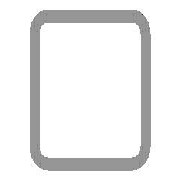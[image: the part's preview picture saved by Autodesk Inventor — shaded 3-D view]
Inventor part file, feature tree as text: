
AUTODESK INVENTOR PART (.ipt)
format: ipt  version: 2025 (Build 290162010, 162A)  size: 143,872 bytes
history: native  units: mm (DEFAULTED — no unit token found)
features: other x3, sketch x1, plane x1
ambient origin geometry x8: Origin, YZ Plane, XZ Plane, XY Plane, X Axis, Y Axis, Z Axis, Center Point
bodies: Solid1 (feature_tree), Body (feature_tree)
feature tree (5):
  other  "Driven Length"
  other  "Start plane"
  other  "End plane"
  sketch  "Sketch3"  dims[d3=2294.0mm d4=0.0mm d7=4.0mm d9=50.0mm d11=50.0mm d12=2.0mm d13=-0.0mm d14=2294.0mm d15=25.0mm d16=25.0mm d17=90.0deg d18=2294.0mm]
  plane  "Work Plane3"
